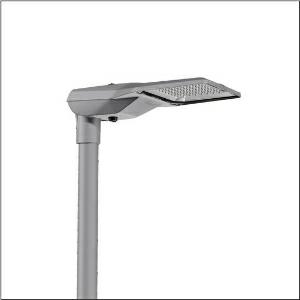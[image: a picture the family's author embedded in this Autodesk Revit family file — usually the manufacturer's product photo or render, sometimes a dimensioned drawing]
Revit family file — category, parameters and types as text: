
# Revit family: streetlight_sl_21_midi___pl52_5xe3h43t08mb_7d48
name_source: partatom
category: Lighting Fixtures
units: mm (PartAtom-declared; Revit-internal decimal feet)

## family parameters
Cut with Voids When Loaded = No
Host = Face
Light Source = No
Part Type = Normal
Room Calculation Point = No
Round Connector Dimension = Use Diameter
Shared = No

## types (1)
- --- (1 x LED, 19830 lm, 147 W, 4000K)
    Apparent Load = 147 VA
    CIE Flux Codes = 27 59 98 100 100
    Color Rendering = 70
    Color Temperature = 4000K
    Default Elevation = 1800 mm
    Description = Streetlight SL 21 midi, mast luminaire, primary light control with lens, of PMMA, primary optical cover: cover, of toughened safety glass, transparent, light distribution: PL52, light emission: direct distribution, primary light characteristic: asymmetric, installation type: side-entry, post-top, LED, High Power LED, rated luminous flux: 19.830lm, luminous efficacy: 135lm/W, light colour: 740, colour temperature: 4000K, control gear: D4i, control: overheat protection, constant luminous flux control, time-dependent luminous flux control, flexible luminous flux parameterisation, pre-setting: logarithmic dimming characteristic, mains connection: 230..240V, AC, 50/60Hz, start of lifetime: 147W, end of service life: 155W, reduction: 65W, luminaire housing, of diecast aluminium, powder-coated, Siteco® metallic grey (DB 702S), corrosivity category C5 mid according to DIN EN ISO 12944, please order mast flange separately, inclination adjustable: 0°, 5°, 10°, 15°, sealing non-destructively replaceable, multi-level sealing system, length: 644mm, width: 335mm, height: 110mm, mast flange for spigot size: 42mm (side-entry): 5XC10008XM4, 60/48mm (side-entry/post-top): 5XC10108XM2, 76/60mm (side-entry/post-top): 5XC10108XM1, mounting height: 4..8m, Smart Interface below and above, protection rating (complete): IP66, insulation class (complete): insulation class II (safety insulation), certification: CE, ENEC, ENEC+, VDE, impact resistance: IK10, permissible operating ambient temperature for outdoor applications: -40..+50°C, standard-compliant lighting for roads and squares, packaging unit: 1 piece

Light Distribution: PL52
    Height = 111 mm
    Lamp = 1 x LED
    Lamp Light Flux = 19830 lm
    Lamp Power = 147 W
    Lamp count = 1
    Length = 644 mm
    Luminous efficacy = 135 lm/W
    Manufacturer = Siteco
    ModVariant = No
    Model = 5XE3H43T08MB
    Number of Poles = 1
    OnlyDefault = Yes
    Power Factor = 1
    Product Name = Streetlight SL 21 midi | PL52
    Product group = mast luminaire | pylon top
    ProductGroupID = 6100
    Protection Class = Protection class II
    Protection Degree = IP 66
    RLX_Detail_Level = 1
    RLX_Emergency_Light_Flux = 0 lm
    RLX_Emergency_Type = 0
    RLX_Emergency_Type_DB = No
    RlxData = <blob elided: 36589 chars, md5=2f5e2823>
    Socket = socket
    Standby Power = 0 W
    System Light Flux = 19830 lm
    System Power = 147 W
    Type Comments = factory setting: luminous flux: 100 % | dim-lin: 254 | 750 mA
    Type Image = l_1004304.jpg
    URL = http://relux.com
    VarID = @adj_190550
    Voltage = 0 V
    Weight = 0.00 kg
    Width = 336 mm

## geometry (parser evidence)
native form markers: Blend x4, Sweep x13
no freeform markers — native parametric forms only
